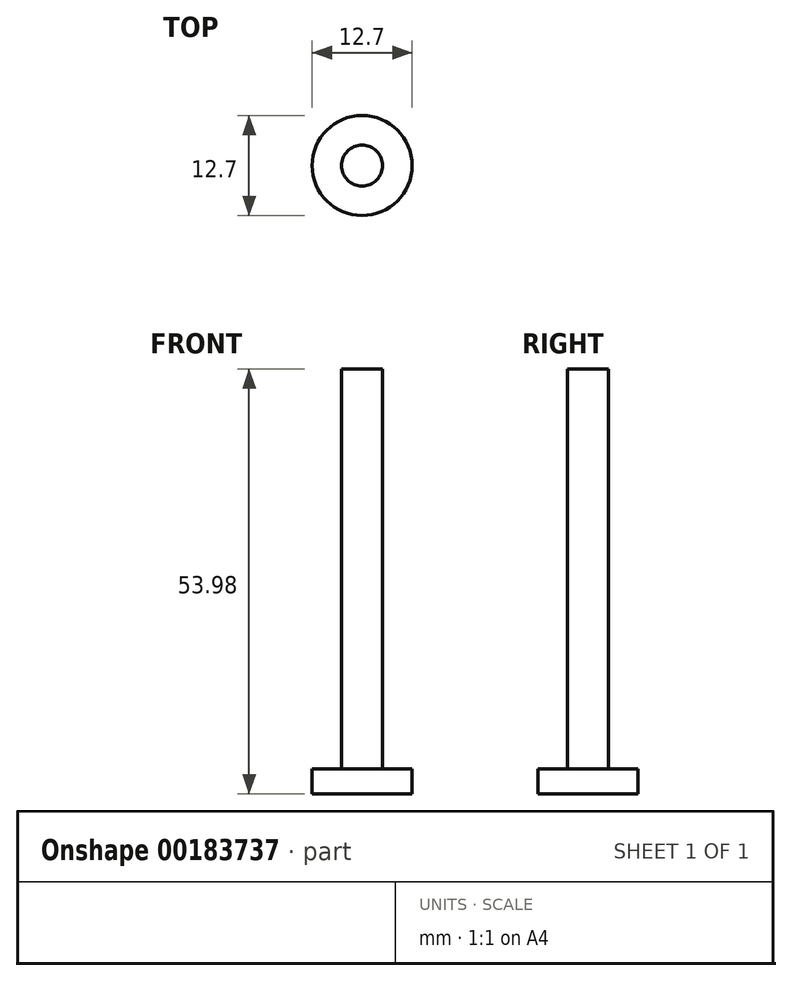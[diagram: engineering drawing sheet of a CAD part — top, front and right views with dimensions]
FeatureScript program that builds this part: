
annotation { "Feature Type Name" : "Feature", "Feature Type Description" : "" }
export const myFeature = defineFeature(function(context is Context, id is Id, definition is map)
    precondition{}
    {
        {
            var Q0;
            Q0=qCreatedBy(makeId("Top.planeOp"),FACE);
            var sketch = newSketch(context, id + "F0", { "sketchPlane" : qUnion([Q0])});
            skCircle(sketch, "E0", {"center": v(0, 0) * mm, "radius": 6.35 * mm});
            skCircle(sketch, "E1", {"center": v(0, 0) * mm, "radius": 2.6 * mm});
            skSolve(sketch);
        }
        {
            var Q0;
            Q0=makeQuery(id+"F0.imprint","IMPRINT",FACE,{"disambiguationData":[TD([[makeQuery(id+"F0.imprint","IMPRINT",EDGE,{"derivedFrom":sQuery(id+"F0.wireOp",EDGE,"E0")}),1.0]])]});
            var Q1;
            Q1=makeQuery(id+"F0.imprint","IMPRINT",FACE,{"disambiguationData":[TD([[makeQuery(id+"F0.imprint","IMPRINT",EDGE,{"derivedFrom":sQuery(id+"F0.wireOp",EDGE,"E1")}),1.0]])]});
            extrude(context, id + "F1", {"entities" : qUnion([Q0, Q1]), "depth" : 3.17 * mm});
        }
        {
            var Q0;
            Q0=makeQuery(id+"F1.opExtrude","CAP_FACE",FACE,{"disambiguationData":[OSD([sQuery(id+"F0.wireOp",EDGE,"E0")])],"isStart":false});
            var sketch = newSketch(context, id + "F2", { "sketchPlane" : qUnion([Q0])});
            skCircle(sketch, "E2", {"center": v(0, 0) * mm, "radius": 2.6 * mm});
            skSolve(sketch);
        }
        {
            var Q0;
            Q0 = qSketchRegion(id + "F2", true);
            extrude(context, id + "F3", {"entities" : qUnion([Q0]), "operationType" : NewBodyOperationType.ADD, "depth" : 50.8 * mm});
        }
    });
